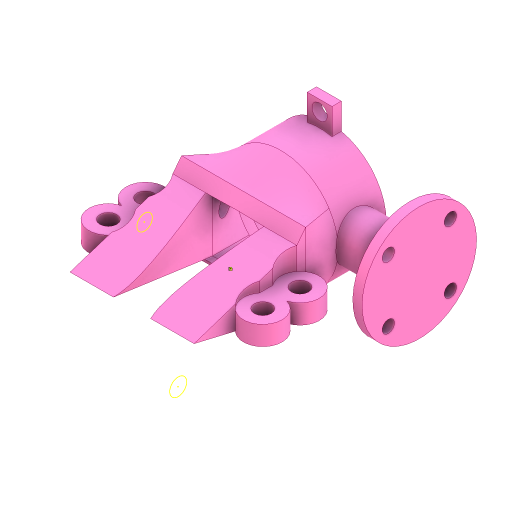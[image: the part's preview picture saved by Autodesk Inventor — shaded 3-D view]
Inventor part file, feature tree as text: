
AUTODESK INVENTOR PART (.ipt)
format: ipt  version: 2024 (Build 280153000, 153)  size: 1,755,136 bytes
history: native  units: mm
features: sketch x24, extrude x19, projected_geometry x11, split x10, other x10, loft x6, boolean_combine x5, plane x4, fillet x2, sweep x2, thicken_offset x2
ambient origin geometry x8: Origin, YZ Plane, XZ Plane, XY Plane, X Axis, Y Axis, Z Axis, Center Point
bodies: Solid1 (feature_tree), Solid2 (feature_tree), Solid19 (feature_tree), Solid20 (feature_tree), Solid21 (feature_tree), Solid22 (feature_tree), Solid23 (feature_tree), Solid3 (feature_tree), Solid4 (feature_tree), Solid5 (feature_tree), Solid6 (feature_tree), Solid7 (feature_tree), Solid8 (feature_tree), Solid9 (feature_tree), Solid10 (feature_tree), Solid11 (feature_tree), Solid12 (feature_tree), Solid13 (feature_tree), Solid14 (feature_tree), Solid15 (feature_tree), Solid16 (feature_tree), Solid17 (feature_tree), Solid18 (feature_tree)
feature tree (95):
  extrude  "Extrusion1"  Depth=3.0mm TaperAngle=0.0deg
  extrude  "Extrusion2"  Depth=3.0mm TaperAngle=0.0deg
  extrude  "Extrusion3"  Depth=40.0mm
  plane  "Work Plane2"
  sketch  "Sketch4"  dims[d4=29.0mm d5=3.0mm d6=0.0mm]
  loft  "Loft1"
  loft  "Loft2"
  loft  "Loft3"
  loft  "Loft4"
  boolean_combine  "Combine1"
  loft  "Loft5"
  fillet  "Fillet1"  [1 undecoded]
  fillet  "Fillet2"  [1 undecoded]
  plane  "Work Plane3"
  extrude  "Extrusion5"  TaperAngle=0.0deg  [1 undecoded]
  extrude  "Extrusion6"  TaperAngle=0.0deg  [1 undecoded]
  extrude  "Extrusion7"  Depth=40.0mm
  extrude  "Extrusion8"  TaperAngle=0.0deg  [1 undecoded]
  extrude  "Extrusion9"  Depth=2.0mm
  extrude  "Extrusion10"  Depth=38.0mm
  extrude  "Extrusion11"  Depth=3.0mm TaperAngle=0.0deg
  extrude  "Extrusion12"  Depth=3.0mm TaperAngle=0.0deg
  extrude  "Extrusion13"  Depth=12.5mm TaperAngle=0.0deg
  extrude  "Extrusion14"  Depth=3.7mm TaperAngle=0.0deg
  extrude  "Extrusion15"  Depth=8.5mm
  split  "Split1"
  split  "Split2"
  split  "Split3"
  split  "Split4"
  split  "Split5"
  split  "Split6"
  split  "Split7"
  boolean_combine  "Combine2"
  split  "Split8"
  boolean_combine  "Combine3"
  boolean_combine  "Combine4"
  extrude  "Extrusion16"  Depth=8.5mm
  extrude  "Extrusion17"  Depth=2.7mm TaperAngle=0.0deg
  sketch  "Sketch36"  dims[d47=15.0mm d48=3.0mm d49=0.0mm]
  sweep  "Sweep1"
  split  "Split9"
  loft  "Loft6"
  thicken_offset  "Thicken1"
  extrude  "Extrusion18"  Depth=10.0mm TaperAngle=0.0deg
  sweep  "Sweep2"
  split  "Split10"
  thicken_offset  "Thicken2"
  boolean_combine  "Combine5"
  plane  "Work Plane4"
  extrude  "Extrusion19"  Depth=10.0mm
  other  "Work Point1"
  other  "Work Point2"
  other  "Work Point3"
  extrude  "Extrusion20"  Depth=10.0mm
  sketch  "Sketch1"  dims[d0=3.0mm d1=0.0mm d2=9.5mm d3=0.0mm]
  plane  "Work Plane1"
  other  "2D Equation Curve1"
  other  "Edges1"
  other  "Edges2"
  other  "Edges3"
  other  "Edges4"
  sketch  "Sketch7"  dims[d7=12.0mm d8=36.0mm d9=40.0mm]
  sketch  "Sketch10"  dims[d10=9.0mm d11=10.0mm]
  sketch  "Sketch12"  dims[d12=3.0mm d13=-6.0mm d14=6.0mm]
  sketch  "Sketch13"  dims[d15=40.0mm d16=26.0mm]
  sketch  "Sketch16"  dims[d17=20.0mm d18=20.0mm]
  projected_geometry  "Projected Loop1"
  sketch  "Sketch18"  dims[d19=0.0mm d20=90.0deg d21=0.0mm d22=90.0deg d23=0.0mm d24=90.0deg d25=0.0mm d26=90.0deg]
  sketch  "Sketch19"  dims[d27=0.0mm d28=90.0deg d29=0.0mm d30=90.0deg]
  projected_geometry  "Projected Loop2"
  projected_geometry  "Projected Loop3"
  projected_geometry  "Projected Loop4"
  projected_geometry  "Projected Loop5"
  sketch  "Sketch23"  dims[d31=0.0mm d32=90.0deg d33=0.0mm d34=90.0deg]
  sketch  "Sketch24"  dims[d35=26.0mm d36=40.0mm]
  sketch  "Sketch28"  dims[d37=4.0mm d38=0.0mm d39=90.0deg]
  sketch  "Sketch29"  dims[d40=0.0mm d41=90.0deg d42=2.0mm]
  sketch  "Sketch35"  dims[d43=1.5mm d46=38.0mm]
  projected_geometry  "Projected Loop11"
  sketch  "3D Sketch2"
  other  "Srf1"
  sketch  "Sketch38"  dims[d50=15.0mm d51=3.0mm d52=0.0mm]
  projected_geometry  "Projected Loop12"
  sketch  "Sketch42"  dims[d53=11.0mm d54=12.5mm d55=0.0mm]
  projected_geometry  "Projected Loop19"
  projected_geometry  "Projected Loop20"
  sketch  "Sketch43"  dims[d56=11.0mm d57=3.7mm d58=0.0mm]
  sketch  "Sketch46"  dims[d59=20.0mm d60=0.0mm d61=8.5mm]
  projected_geometry  "Projected Loop21"
  sketch  "3D Sketch3"
  sketch  "Sketch47"  dims[d62=8.5mm d63=8.5mm]
  projected_geometry  "Projected Loop22"
  sketch  "Sketch49"  dims[d64=8.5mm d65=2.7mm d66=0.0mm]
  sketch  "Sketch50"  dims[d67=40.0mm d68=10.0mm d69=2.7mm d70=0.0mm d71=2.5mm d72=0.0mm d73=2.5mm d74=0.0mm d75=9.0mm d76=2.0mm d77=0.0mm d78=0.0mm d79=7.0mm d80=5.5mm d81=8.5mm d82=8.5mm d83=2.5mm d84=0.0mm d85=2.5mm d86=0.0mm d87=0.5mm d88=0.0mm d89=0.0mm d91=10.0mm d92=10.0mm d93=0.1mm d94=0.0mm d95=16.0mm d96=2.5mm d97=4.0mm d98=2.5mm d99=2.5mm d100=5.0mm d101=5.0mm d102=2.5mm d103=2.5mm d104=2.5mm d105=2.5mm d106=0.0mm d107=0.0mm d108=2.5mm d109=2.5mm d110=0.0mm d111=90.0deg d112=0.0mm d113=90.0deg d114=0.1mm d115=0.1mm d116=0.1mm d117=0.0mm d118=15.0mm d119=3.0mm d120=1.6mm d121=1.5mm d122=16.5mm d125=5.5mm d126=2.5mm d127=2.5mm d128=0.0mm d129=0.0mm d130=0.1mm d131=0.1mm d132=58.25mm d133=6.0mm d134=16.0mm d135=0.0mm d136=12.0mm d137=12.0mm d138=12.0mm d139=12.0mm d140=10.0mm d141=0.0mm]
  other  "Unwrap1"
note: 5 required parameter values undecoded (feature->parameter linkage not recoverable at this tier; creation-order binding heuristic only, values carry confidence <= 0.55)
